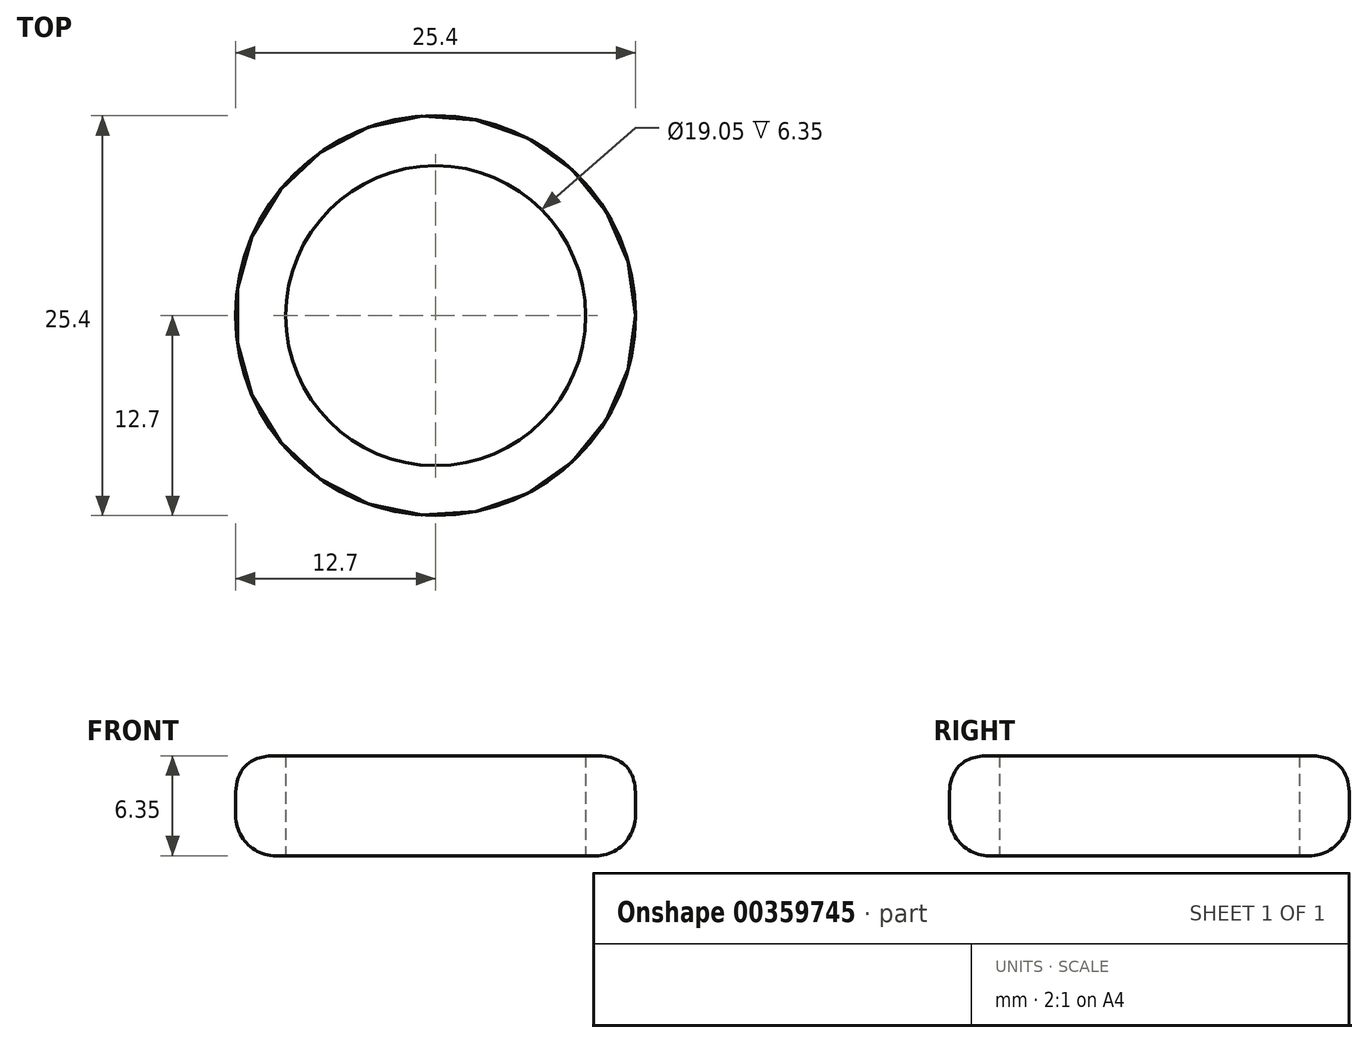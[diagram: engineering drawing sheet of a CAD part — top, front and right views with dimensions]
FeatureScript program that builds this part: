
annotation { "Feature Type Name" : "Feature", "Feature Type Description" : "" }
export const myFeature = defineFeature(function(context is Context, id is Id, definition is map)
    precondition{}
    {
        {
            var Q0;
            Q0=qCreatedBy(makeId("Top.planeOp"),FACE);
            var sketch = newSketch(context, id + "F0", { "sketchPlane" : qUnion([Q0])});
            skCircle(sketch, "E0", {"center": v(0, 0) * mm, "radius": 12.7 * mm});
            skSolve(sketch);
        }
        {
            var Q0;
            Q0=makeQuery(id+"F0.imprint","IMPRINT",FACE,{"disambiguationData":[TD([[makeQuery(id+"F0.imprint","IMPRINT",EDGE,{"derivedFrom":sQuery(id+"F0.wireOp",EDGE,"E0")}),1.0]])]});
            extrude(context, id + "F1", {"entities" : qUnion([Q0]), "depth" : 6.35 * mm});
        }
        {
            var Q0;
            Q0=makeQuery(id+"F1.opExtrude","CAP_FACE",FACE,{"disambiguationData":[OSD([sQuery(id+"F0.wireOp",EDGE,"E0")])],"isStart":true});
            var sketch = newSketch(context, id + "F2", { "sketchPlane" : qUnion([Q0])});
            skCircle(sketch, "E1", {"center": v(0, 0) * mm, "radius": 9.53 * mm});
            skSolve(sketch);
        }
        {
            var Q0;
            Q0=makeQuery(id+"F2.imprint","IMPRINT",FACE,{"disambiguationData":[TD([[makeQuery(id+"F2.imprint","IMPRINT",EDGE,{"derivedFrom":sQuery(id+"F2.wireOp",EDGE,"E1")}),1.0]])]});
            extrude(context, id + "F3", {"entities" : qUnion([Q0]), "operationType" : NewBodyOperationType.REMOVE, "oppositeDirection" : true, "depth" : 6.35 * mm});
        }
        {
            var Q0;
            Q0=makeQuery(id+"F1.opExtrude","CAP_EDGE",EDGE,{"disambiguationData":[OSD([sQuery(id+"F0.wireOp",EDGE,"E0")])],"isStart":false});
            fillet(context, id + "F4", {"entities" : qUnion([Q0]), "radius" : 2.54 * mm, "tangentPropagation" : true, "rho" : 0.5, "crossSection" : FilletCrossSection.CONIC, "allowEdgeOverflow" : false});
        }
        {
            var Q0;
            Q0=makeQuery(id+"F1.opExtrude","SWEPT_FACE",FACE,{"disambiguationData":[OSD([sQuery(id+"F0.wireOp",EDGE,"E0")])]});
            fillet(context, id + "F5", {"entities" : qUnion([Q0]), "radius" : 2.54 * mm, "tangentPropagation" : true, "allowEdgeOverflow" : false});
        }
    });
